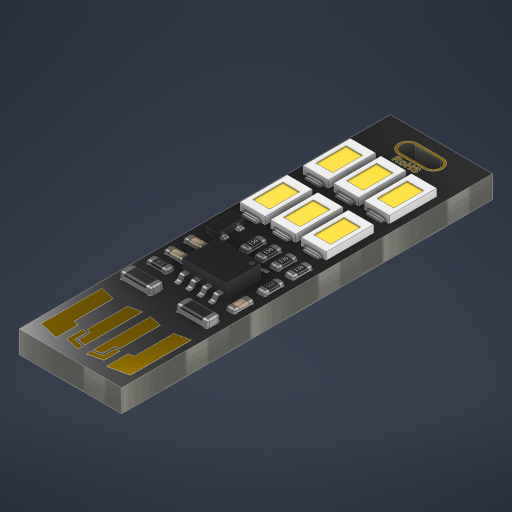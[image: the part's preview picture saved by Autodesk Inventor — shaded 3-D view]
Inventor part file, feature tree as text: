
AUTODESK INVENTOR PART (.ipt)
format: ipt  version: 2024 (Build 280153020, 153B)  size: 5,390,848 bytes
history: native  units: mm
features: other x31, extrude x27, move_body x13, sketch x12, fillet x12, projected_geometry x10, plane x1, mirror x1
ambient origin geometry x8: Origin, YZ Plane, XZ Plane, XY Plane, X Axis, Y Axis, Z Axis, Center Point
bodies: Solid1 (feature_tree), Solid2 (feature_tree), Solid3 (feature_tree), Solid4 (feature_tree), Solid5 (feature_tree), Solid6 (feature_tree), Solid7 (feature_tree), Solid1_1 (feature_tree), Solid1_2 (feature_tree), Solid1_3 (feature_tree), Solid1_4 (feature_tree), Solid1_5 (feature_tree), Solid1_6 (feature_tree), Solid1_7 (feature_tree), Solid1_8 (feature_tree), Solid1_9 (feature_tree), Solid1_10 (feature_tree), Solid1_11 (feature_tree), Solid1_12 (feature_tree), Solid1_13 (feature_tree)
feature tree (107):
  other  "Transistor_3-leg.ipt"
  other  "MicroResistor.ipt"
  other  "MicroResistor_noPrint.ipt"
  other  "8-PinRectangleChip.ipt"
  other  "MicroResistor-LittleLarger.ipt"
  extrude  "Extrusion1"  Depth=42.62mm
  sketch  "Sketch2"  dims[d2=4.57mm d3=1.68mm]
  extrude  "Extrusion2"  Depth=1.68mm
  extrude  "Extrusion3"  Depth=2.58mm TaperAngle=0.0deg
  extrude  "Extrusion4"  Depth=5.45mm
  extrude  "Extrusion5"  Depth=5.5mm
  extrude  "Extrusion6"  Depth=2.91mm
  extrude  "Extrusion7"  Depth=2.91mm
  sketch  "Sketch3"  dims[d4=1.56mm d5=2.58mm d6=0.0mm]
  extrude  "Extrusion8"  Depth=0.6mm
  extrude  "Extrusion9"  Depth=0.85mm TaperAngle=0.0deg
  extrude  "Extrusion10"  Depth=0.85mm TaperAngle=0.0deg
  extrude  "Extrusion11"  Depth=0.85mm TaperAngle=0.0deg
  extrude  "Extrusion12"  Depth=1.85mm
  extrude  "Extrusion13"  Depth=0.45mm
  fillet  "Fillet1"  Radius=1.85mm
  fillet  "Fillet2"  Radius=1.85mm
  fillet  "Fillet3"  Radius=1.85mm
  fillet  "Fillet4"  Radius=1.85mm
  fillet  "Fillet5"  Radius=1.85mm
  fillet  "Fillet6"  Radius=1.85mm
  fillet  "Fillet7"  Radius=1.85mm
  fillet  "Fillet8"  Radius=1.85mm
  fillet  "Fillet9"  Radius=1.85mm
  fillet  "Fillet10"  Radius=1.85mm
  fillet  "Fillet11"  Radius=1.85mm
  fillet  "Fillet12"  Radius=0.25mm
  sketch  "Sketch4"  dims[d7=2.91mm d8=5.45mm]
  extrude  "Extrusion14"  Depth=0.25mm TaperAngle=0.0deg
  extrude  "Extrusion15"  Depth=0.25mm TaperAngle=0.0deg
  extrude  "Extrusion16"  Depth=0.25mm TaperAngle=0.0deg
  extrude  "Extrusion17"  Depth=0.25mm TaperAngle=0.0deg
  extrude  "Extrusion18"  Depth=0.25mm TaperAngle=0.0deg
  extrude  "Extrusion19"  Depth=0.2mm
  move_body  "Move Body1"
  move_body  "Move Body2"
  move_body  "Move Body3"
  move_body  "Move Body4"
  move_body  "Move Body5"
  move_body  "Move Body6"
  move_body  "Move Body7"
  move_body  "Move Body8"
  extrude  "Extrusion20"  Depth=0.2mm
  extrude  "Extrusion21"  Depth=0.2mm
  move_body  "Move Body9"
  extrude  "Extrusion22"  Depth=0.2mm
  move_body  "Move Body10"
  move_body  "Move Body11"
  extrude  "Extrusion23"  Depth=0.2mm
  extrude  "Extrusion24"  Depth=0.2mm
  move_body  "Move Body12"
  move_body  "Move Body13"
  extrude  "Extrusion25"  Depth=0.2mm
  plane  "Work Plane1"
  mirror  "Mirror1"
  extrude  "Extrusion26"  Depth=0.2mm
  extrude  "Extrusion27"  Depth=0.2mm
  sketch  "Sketch1"  dims[d0=11.76mm d1=42.62mm]
  other  "Solid1::Transistor_3-leg.ipt"
  other  "TaggingFeature1"
  other  "Solid1::MicroResistor.ipt"
  other  "TaggingFeature2"
  other  "Solid1::MicroResistor.ipt_1"
  other  "TaggingFeature3"
  other  "Solid1::MicroResistor.ipt_2"
  other  "TaggingFeature4"
  other  "Solid1::MicroResistor.ipt_3"
  other  "TaggingFeature5"
  other  "Solid1::MicroResistor.ipt_4"
  other  "TaggingFeature6"
  other  "Solid1::MicroResistor_noPrint.ipt"
  other  "TaggingFeature7"
  other  "Solid1::MicroResistor_noPrint.ipt_1"
  other  "TaggingFeature8"
  sketch  "Sketch5"  dims[d9=0.91mm d10=5.5mm]
  projected_geometry  "Projected Loop1"
  projected_geometry  "Projected Loop2"
  projected_geometry  "Projected Loop3"
  sketch  "Sketch6"  dims[d11=2.91mm d12=5.45mm d13=2.91mm d14=5.45mm]
  other  "Solid1::MicroResistor_noPrint.ipt_2"
  other  "TaggingFeature9"
  sketch  "Sketch7"  dims[d15=2.91mm d16=5.45mm d17=2.91mm d18=5.45mm]
  other  "Solid1::8-PinRectangleChip.ipt"
  other  "TaggingFeature10"
  other  "Solid1::MicroResistor.ipt_5"
  other  "TaggingFeature11"
  sketch  "Sketch8"  dims[d19=2.91mm d20=5.45mm d21=0.6mm d22=0.6mm]
  projected_geometry  "Projected Loop4"
  projected_geometry  "Projected Loop5"
  projected_geometry  "Projected Loop6"
  sketch  "Sketch9"  dims[d23=1.8mm d24=0.85mm d25=0.0mm]
  other  "Solid1::MicroResistor-LittleLarger.ipt"
  other  "TaggingFeature12"
  other  "Solid1::MicroResistor-LittleLarger.ipt_1"
  other  "TaggingFeature13"
  sketch  "Sketch10"  dims[d26=0.85mm d27=0.0mm d28=0.85mm d29=0.0mm]
  sketch  "Sketch11"  dims[d30=0.85mm d31=0.0mm d32=0.85mm d33=0.0mm]
  projected_geometry  "Projected Loop7"
  projected_geometry  "Projected Loop8"
  projected_geometry  "Projected Loop9"
  projected_geometry  "Projected Loop10"
  sketch  "Sketch12"  dims[d34=0.85mm d35=0.0mm d36=1.85mm d37=0.45mm d38=1.85mm d39=0.45mm d40=1.85mm d41=0.45mm d42=1.85mm d43=0.45mm d44=1.85mm d45=0.45mm d46=1.85mm d47=0.45mm d48=1.85mm d49=0.45mm d50=1.85mm d51=0.45mm d52=1.85mm d53=0.45mm d54=1.85mm d55=0.45mm d56=1.85mm d57=0.45mm d58=1.85mm d59=0.45mm d60=0.25mm d61=0.0mm d62=0.25mm d63=0.0mm d64=0.25mm d65=0.0mm d66=0.25mm d67=0.0mm d68=0.25mm d69=0.0mm d70=0.25mm d71=0.0mm d72=0.2mm d73=0.2mm d74=0.2mm d75=0.2mm d76=0.2mm d77=0.2mm d78=0.2mm d79=0.2mm d80=0.2mm d81=0.2mm d82=0.2mm d83=0.2mm d84=0.5mm d85=0.5mm d86=1.0mm d87=1.0mm d88=1.0mm d89=1.0mm d90=0.5mm d91=0.5mm d92=0.5mm d93=0.5mm d94=0.1mm d95=0.0mm d96=0.1mm d97=0.0mm d98=0.1mm d99=0.0mm d100=0.1mm d101=0.0mm d102=0.1mm d103=0.0mm d104=0.1mm d105=0.0mm d106=10.0mm d107=2.58mm d108=1.25mm d109=20.2mm d110=10.0mm d111=90.0deg d112=2.58mm d113=5.5mm d114=20.75mm d115=10.0mm d116=90.0deg d117=2.58mm d118=7.25mm d119=20.75mm d120=10.0mm d121=90.0deg d122=2.58mm d123=9.0mm d124=20.75mm d125=10.0mm d126=90.0deg d127=2.58mm d128=10.75mm d129=20.75mm d130=10.0mm d131=90.0deg d132=2.58mm d133=10.75mm d134=17.5mm d135=10.0mm d136=90.0deg d137=2.58mm d138=10.75mm d139=14.0mm d140=10.0mm d141=2.58mm d142=1.0mm d143=18.25mm d144=0.1mm d145=0.0mm d146=0.02mm d147=0.0mm d148=10.0mm d149=2.58mm d150=1.0mm d151=16.0mm d152=0.25mm d153=0.1mm d154=3.25mm d155=0.9mm d156=0.02mm d157=0.0mm d158=10.0mm d159=2.58mm d160=4.0mm d161=14.75mm d162=10.0mm d163=2.58mm d164=1.0mm d165=14.0mm d166=0.02mm d167=0.0mm d168=0.375mm d169=0.85mm d170=0.02mm d171=0.0mm d172=10.0mm d173=2.58mm d174=1.25mm d175=10.75mm d176=10.0mm d177=2.58mm d178=7.75mm d179=10.75mm d180=1.65mm d181=2.25mm d182=0.75mm d184=1.0mm d185=1.4mm d186=0.25mm d187=0.25mm d188=0.25mm d189=1.25mm d190=1.35mm d191=0.5mm d192=0.5mm d193=2.5mm d194=7.0mm d195=1.75mm d196=0.75mm d197=13.526302mm d198=0.02mm d199=0.0mm d200=0.02mm d201=0.0mm d202=11.0mm d203=1.333664mm d204=1.333664mm d205=10.824624mm d206=10.824624mm d207=20.231237mm d208=20.266721mm d209=1.333664mm d210=2.0mm d211=0.561598mm d212=0.85mm d213=0.2mm d214=0.2mm d215=0.02mm d216=0.0mm]
